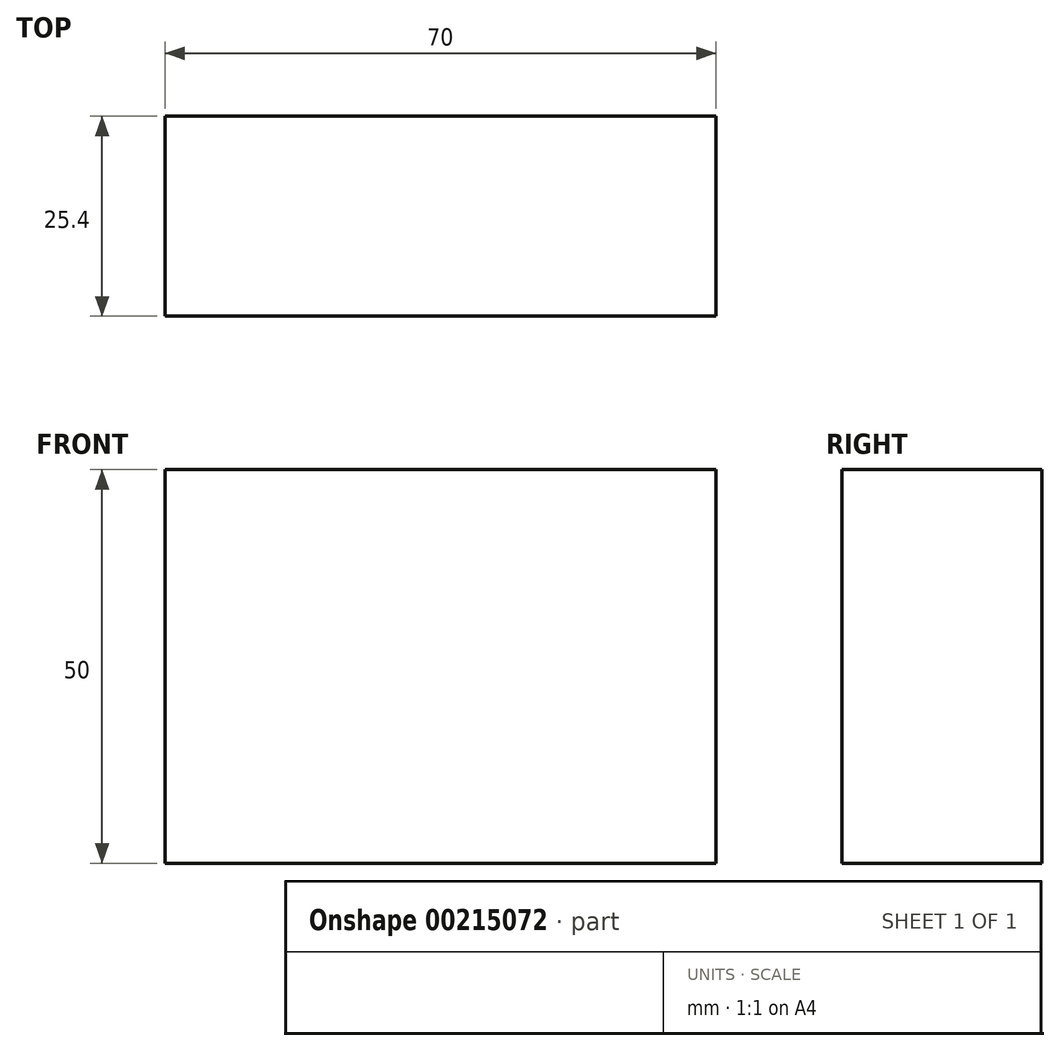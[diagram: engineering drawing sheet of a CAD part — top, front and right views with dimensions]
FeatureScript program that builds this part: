
annotation { "Feature Type Name" : "Feature", "Feature Type Description" : "" }
export const myFeature = defineFeature(function(context is Context, id is Id, definition is map)
    precondition{}
    {
        {
            var Q0;
            Q0=qCreatedBy(makeId("Front.planeOp"),FACE);
            var sketch = newSketch(context, id + "F0", { "sketchPlane" : qUnion([Q0])});
            skLineSegment(sketch, "E0.bottom", {"start": v(0, 0) * mm, "end": v(70, 0) * mm});
            skLineSegment(sketch, "E0.top", {"start": v(0, 50) * mm, "end": v(70, 50) * mm});
            skLineSegment(sketch, "E0.left", {"start": v(0, 0) * mm, "end": v(0, 50) * mm});
            skLineSegment(sketch, "E0.right", {"start": v(70, 0) * mm, "end": v(70, 50) * mm});
            skSolve(sketch);
        }
        {
            var Q0;
            Q0 = qSketchRegion(id + "F0", true);
            extrude(context, id + "F1", {"entities" : qUnion([Q0]), "depth" : 25.4 * mm, "offsetDistance" : 25 * mm});
        }
    });
